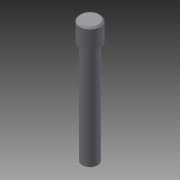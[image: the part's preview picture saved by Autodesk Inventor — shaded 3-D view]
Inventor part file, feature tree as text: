
AUTODESK INVENTOR PART (.ipt)
format: ipt  version: 2014 SP1 (Build 180222100, 222)  size: 89,088 bytes
history: native  units: in
note: dims shown in document units (in); Inventor stores cm internally (conversion verified against a paired STEP export)
features: revolve x1, chamfer x1, sketch x1
ambient origin geometry x8: Origin, YZ Plane, XZ Plane, XY Plane, X Axis, Y Axis, Z Axis, Center Point
bodies: Solid1 (feature_tree)
feature tree (3):
  revolve  "Revolution1"  [1 undecoded]
  chamfer  "Chamfer1"  Distance=0.122in
  sketch  "Sketch1"  dims[d0=0.13in d1=0.0975in d2=0.122in d3=0.773in d4=90.0deg d5=0.01in d6=0.125in d7=45.0deg d8=0.005in]
note: 1 required parameter value undecoded (feature->parameter linkage not recoverable at this tier; creation-order binding heuristic only, values carry confidence <= 0.55)
